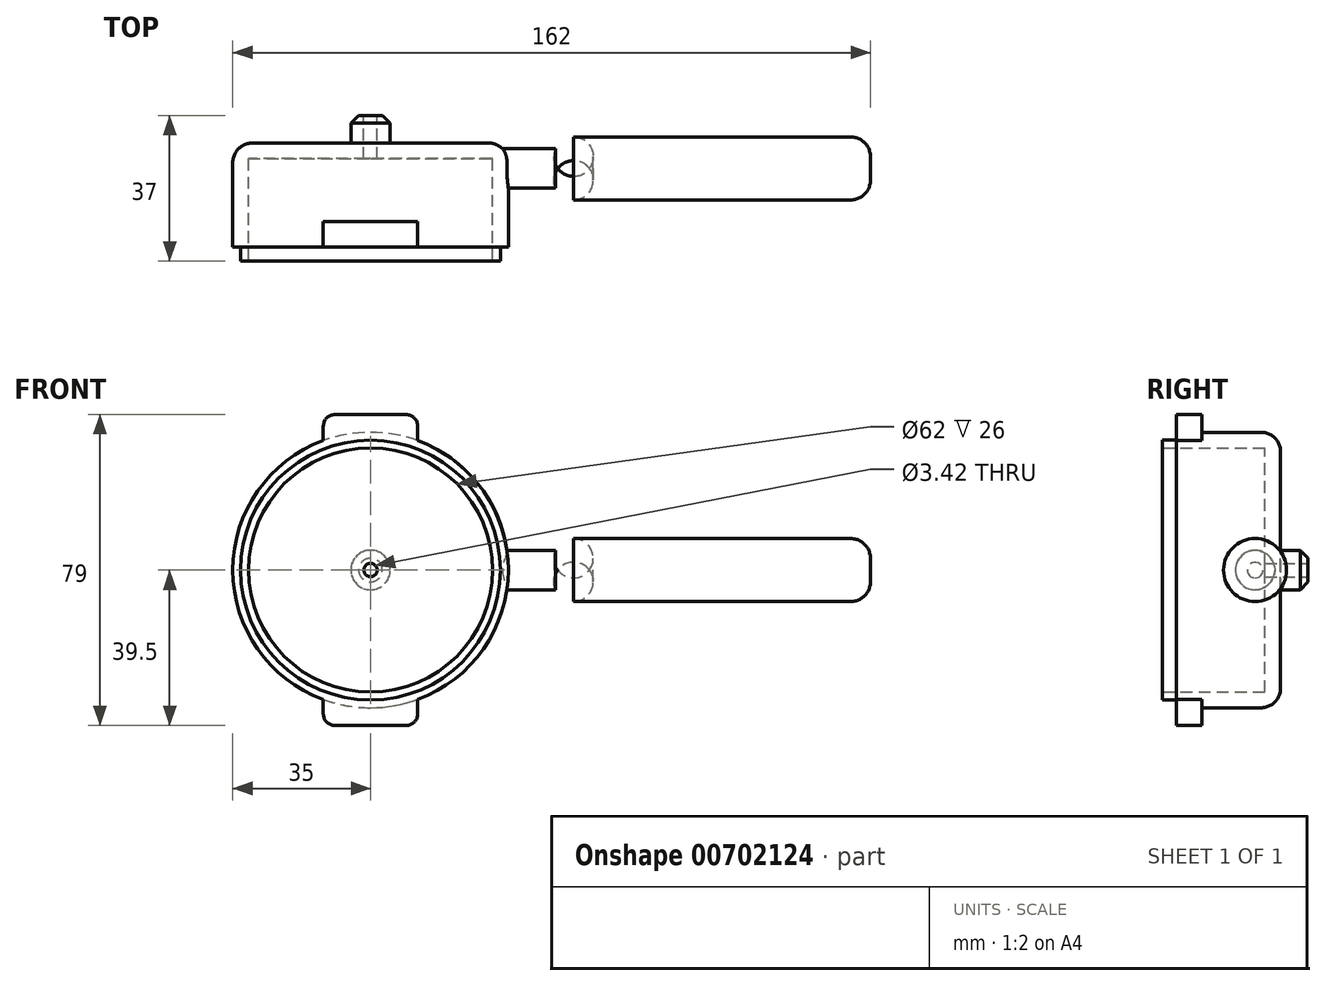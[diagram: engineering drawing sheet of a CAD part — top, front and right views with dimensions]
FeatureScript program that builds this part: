
annotation { "Feature Type Name" : "Feature", "Feature Type Description" : "" }
export const myFeature = defineFeature(function(context is Context, id is Id, definition is map)
    precondition{}
    {
        {
            var Q0;
            Q0=qCreatedBy(makeId("Front.planeOp"),FACE);
            var sketch = newSketch(context, id + "F0", { "sketchPlane" : qUnion([Q0])});
            skCircle(sketch, "E0", {"center": v(0, 0) * mm, "radius": 35 * mm});
            skSolve(sketch);
        }
        {
            var Q0;
            Q0=makeQuery(id+"F0.imprint","IMPRINT",FACE,{"disambiguationData":[TD([[makeQuery(id+"F0.imprint","IMPRINT",EDGE,{"derivedFrom":sQuery(id+"F0.wireOp",EDGE,"E0")}),1.0]])]});
            extrude(context, id + "F1", {"entities" : qUnion([Q0]), "depth" : 30 * mm, "offsetDistance" : 25 * mm});
        }
        {
            var Q0;
            Q0=makeQuery(id+"F1.opExtrude","CAP_FACE",FACE,{"disambiguationData":[OSD([sQuery(id+"F0.wireOp",EDGE,"E0")])],"isStart":false});
            shell(context, id + "F2", {"entities" : qUnion([Q0]), "thickness" : 4 * mm});
        }
        {
            var Q0;
            Q0=makeQuery(id+"F1.opExtrude","CAP_EDGE",EDGE,{"disambiguationData":[OSD([sQuery(id+"F0.wireOp",EDGE,"E0")])],"isStart":true});
            fillet(context, id + "F3", {"entities" : qUnion([Q0]), "radius" : 5 * mm, "tangentPropagation" : true, "allowEdgeOverflow" : false});
        }
        {
            var Q0;
            Q0=qCreatedBy(makeId("Right.planeOp"),FACE);
            cPlane(context, id + "F4", {"entities" : qUnion([Q0]), "cplaneType" : CPlaneType.OFFSET, "offset" : 47 * mm, "width" : 150 * mm, "height" : 150 * mm});
        }
        {
            var Q0;
            Q0=qCreatedBy(id+"F4.planeOp",FACE);
            var sketch = newSketch(context, id + "F5", { "sketchPlane" : qUnion([Q0])});
            skCircle(sketch, "E1", {"center": v(-6.47, 0) * mm, "radius": 5 * mm});
            skSolve(sketch);
        }
        {
            var Q0;
            Q0=makeQuery(id+"F5.imprint","IMPRINT",FACE,{"disambiguationData":[TD([[makeQuery(id+"F5.imprint","IMPRINT",EDGE,{"derivedFrom":sQuery(id+"F5.wireOp",EDGE,"E1")}),1.0]])]});
            extrude(context, id + "F6", {"entities" : qUnion([Q0]), "operationType" : NewBodyOperationType.ADD, "endBound" : BoundingType.UP_TO_NEXT, "oppositeDirection" : true, "depth" : 25 * mm, "offsetDistance" : 25 * mm});
        }
        {
            var Q0;
            Q0=makeQuery(id+"F6.opExtrude","CAP_FACE",FACE,{"disambiguationData":[OSD([sQuery(id+"F5.wireOp",EDGE,"E1")])],"isStart":true});
            var sketch = newSketch(context, id + "F7", { "sketchPlane" : qUnion([Q0])});
            skCircle(sketch, "E2", {"center": v(-6.47, 0) * mm, "radius": 8 * mm});
            skSolve(sketch);
        }
        {
            var Q0;
            Q0=makeQuery(id+"F7.imprint","IMPRINT",FACE,{"disambiguationData":[TD([[makeQuery(id+"F7.imprint","IMPRINT",EDGE,{"derivedFrom":makeQuery(id+"F6.opExtrude","CAP_EDGE",EDGE,{"disambiguationData":[OSD([sQuery(id+"F5.wireOp",EDGE,"E1")])],"isStart":true})}),1.0]])]});
            var Q1;
            Q1=makeQuery(id+"F7.imprint","IMPRINT",FACE,{"disambiguationData":[TD([[makeQuery(id+"F7.imprint","IMPRINT",EDGE,{"derivedFrom":sQuery(id+"F7.wireOp",EDGE,"E2")}),1.0]])]});
            extrude(context, id + "F8", {"entities" : qUnion([Q0, Q1]), "operationType" : NewBodyOperationType.ADD, "depth" : 80 * mm, "offsetDistance" : 25 * mm});
        }
        {
            var Q0;
            Q0=makeQuery(id+"F1.opExtrude","CAP_FACE",FACE,{"disambiguationData":[OSD([sQuery(id+"F0.wireOp",EDGE,"E0")])],"isStart":true});
            var sketch = newSketch(context, id + "F9", { "sketchPlane" : qUnion([Q0])});
            skCircle(sketch, "E3", {"center": v(0, 0) * mm, "radius": 5 * mm});
            skSolve(sketch);
        }
        {
            var Q0;
            Q0=makeQuery(id+"F9.imprint","IMPRINT",FACE,{"disambiguationData":[TD([[makeQuery(id+"F9.imprint","IMPRINT",EDGE,{"derivedFrom":sQuery(id+"F9.wireOp",EDGE,"E3")}),1.0]])]});
            extrude(context, id + "F10", {"entities" : qUnion([Q0]), "operationType" : NewBodyOperationType.ADD, "depth" : 7 * mm, "offsetDistance" : 25 * mm});
        }
        {
            var Q0;
            Q0=makeQuery(id+"F10.opExtrude","CAP_EDGE",EDGE,{"disambiguationData":[OSD([sQuery(id+"F9.wireOp",EDGE,"E3")])],"isStart":false});
            chamfer(context, id + "F11", {"entities" : qUnion([Q0]), "width" : 2 * mm, "tangentPropagation" : true});
        }
        {
            var Q0;
            Q0=makeQuery(id+"F1.opExtrude","CAP_FACE",FACE,{"disambiguationData":[OSD([sQuery(id+"F0.wireOp",EDGE,"E0")])],"isStart":false});
            cPlane(context, id + "F12", {"entities" : qUnion([Q0]), "cplaneType" : CPlaneType.OFFSET, "offset" : 3.5 * mm, "oppositeDirection" : true, "width" : 150 * mm, "height" : 150 * mm});
        }
        {
            var Q0;
            Q0=qCreatedBy(id+"F12.planeOp",FACE);
            var sketch = newSketch(context, id + "F13", { "sketchPlane" : qUnion([Q0])});
            skArc(sketch, "E4.0", {"start": v(12, 32.88) * mm, "mid": v(0, 35) * mm, "end": v(-12, 32.88) * mm});
            skLineSegment(sketch, "E5", {"start": v(0, 0) * mm, "end": v(-35, 0) * mm});
            skLineSegment(sketch, "E6", {"start": v(12, 39.5) * mm, "end": v(-12, 39.5) * mm});
            skLineSegment(sketch, "E7", {"start": v(12, 39.5) * mm, "end": v(12, 32.88) * mm});
            skLineSegment(sketch, "E8", {"start": v(-12, 39.5) * mm, "end": v(-12, 32.88) * mm});
            skPoint(sketch, "E9.orphan", {"position": v(3.01, 0) * mm});
            skLineSegment(sketch, "E10.MirrorCS", {"start": v(12, -39.5) * mm, "end": v(12, -32.88) * mm});
            skLineSegment(sketch, "E11.MirrorCS", {"start": v(12, -39.5) * mm, "end": v(-12, -39.5) * mm});
            skLineSegment(sketch, "E12.MirrorCS", {"start": v(-12, -39.5) * mm, "end": v(-12, -32.88) * mm});
            skArc(sketch, "E13.MirrorCS", {"start": v(12, -32.88) * mm, "mid": v(0, -35) * mm, "end": v(-12, -32.88) * mm});
            skSolve(sketch);
        }
        {
            var Q0;
            Q0=makeQuery(id+"F13.imprint","IMPRINT",FACE,{"disambiguationData":[TD([[makeQuery(id+"F13.imprint","IMPRINT",EDGE,{"derivedFrom":sQuery(id+"F13.wireOp",EDGE,"E10.MirrorCS")}),1.0]])]});
            var Q1;
            Q1=makeQuery(id+"F13.imprint","IMPRINT",FACE,{"disambiguationData":[TD([[makeQuery(id+"F13.imprint","IMPRINT",EDGE,{"derivedFrom":sQuery(id+"F13.wireOp",EDGE,"E4.0")}),-1.0]])]});
            extrude(context, id + "F14", {"entities" : qUnion([Q0, Q1]), "operationType" : NewBodyOperationType.ADD, "oppositeDirection" : true, "depth" : 6.5 * mm, "offsetDistance" : 25 * mm});
        }
        {
            var Q0;
            Q0=makeQuery(id+"F8.opExtrude","CAP_EDGE",EDGE,{"disambiguationData":[OSD([sQuery(id+"F7.wireOp",EDGE,"E2")])],"isStart":false});
            fillet(context, id + "F15", {"entities" : qUnion([Q0]), "radius" : 5 * mm, "tangentPropagation" : true, "allowEdgeOverflow" : false});
        }
        {
            var Q0;
            Q0=makeQuery(id+"F8.opExtrude","CAP_EDGE",EDGE,{"disambiguationData":[OSD([sQuery(id+"F7.wireOp",EDGE,"E2")])],"isStart":true});
            fillet(context, id + "F16", {"entities" : qUnion([Q0]), "radius" : 5 * mm, "tangentPropagation" : true, "allowEdgeOverflow" : false});
        }
        {
            var Q0;
            Q0=makeQuery(id+"F1.opExtrude","CAP_FACE",FACE,{"disambiguationData":[OSD([sQuery(id+"F0.wireOp",EDGE,"E0")])],"isStart":false});
            var sketch = newSketch(context, id + "F17", { "sketchPlane" : qUnion([Q0])});
            skCircle(sketch, "E14", {"center": v(0, 0) * mm, "radius": 33 * mm});
            skCircle(sketch, "E15.0", {"center": v(0, 0) * mm, "radius": 35 * mm});
            skSolve(sketch);
        }
        {
            var Q0;
            Q0=makeQuery(id+"F17.imprint","IMPRINT",FACE,{"disambiguationData":[TD([[makeQuery(id+"F17.imprint","IMPRINT",EDGE,{"derivedFrom":sQuery(id+"F17.wireOp",EDGE,"E14")}),-1.0]])]});
            var Q1;
            Q1=makeQuery(id+"F14.opExtrude","CAP_FACE",FACE,{"disambiguationData":[OSD([sQuery(id+"F13.wireOp",EDGE,"E4.0"),sQuery(id+"F13.wireOp",EDGE,"E6"),sQuery(id+"F13.wireOp",EDGE,"E7"),sQuery(id+"F13.wireOp",EDGE,"E8")])],"isStart":true});
            extrude(context, id + "F18", {"entities" : qUnion([Q0]), "operationType" : NewBodyOperationType.REMOVE, "endBound" : BoundingType.UP_TO_SURFACE, "oppositeDirection" : true, "depth" : 25 * mm, "endBoundEntityFace" : qUnion([Q1]), "offsetDistance" : 25 * mm});
        }
        {
            var Q0;
            Q0=makeQuery(id+"F14.opExtrude","SWEPT_EDGE",EDGE,{"disambiguationData":[OSD([sQuery(id+"F13.wireOp",EDGE,"E6"),sQuery(id+"F13.wireOp",EDGE,"E7")])]});
            var Q1;
            Q1=makeQuery(id+"F14.opExtrude","SWEPT_EDGE",EDGE,{"disambiguationData":[OSD([sQuery(id+"F13.wireOp",EDGE,"E6"),sQuery(id+"F13.wireOp",EDGE,"E8")])]});
            var Q2;
            Q2=makeQuery(id+"F14.opExtrude","SWEPT_EDGE",EDGE,{"disambiguationData":[OSD([sQuery(id+"F13.wireOp",EDGE,"E11.MirrorCS"),sQuery(id+"F13.wireOp",EDGE,"E12.MirrorCS")])]});
            var Q3;
            Q3=makeQuery(id+"F14.opExtrude","SWEPT_EDGE",EDGE,{"disambiguationData":[OSD([sQuery(id+"F13.wireOp",EDGE,"E10.MirrorCS"),sQuery(id+"F13.wireOp",EDGE,"E11.MirrorCS")])]});
            fillet(context, id + "F19", {"entities" : qUnion([Q0, Q1, Q2, Q3]), "radius" : 3 * mm, "tangentPropagation" : true, "allowEdgeOverflow" : false});
        }
        {
            var Q0;
            Q0=makeQuery(id+"F10.opExtrude","CAP_FACE",FACE,{"disambiguationData":[OSD([sQuery(id+"F9.wireOp",EDGE,"E3")])],"isStart":false});
            var sketch = newSketch(context, id + "F20", { "sketchPlane" : qUnion([Q0])});
            skCircle(sketch, "E16", {"center": v(0, 0) * mm, "radius": 1.7 * mm});
            skSolve(sketch);
        }
        {
            var Q0;
            Q0=makeQuery(id+"F20.imprint","IMPRINT",FACE,{"disambiguationData":[TD([[makeQuery(id+"F20.imprint","IMPRINT",EDGE,{"derivedFrom":sQuery(id+"F20.wireOp",EDGE,"E16")}),1.0]])]});
            extrude(context, id + "F21", {"entities" : qUnion([Q0]), "operationType" : NewBodyOperationType.REMOVE, "endBound" : BoundingType.THROUGH_ALL, "oppositeDirection" : true, "depth" : 25 * mm, "offsetDistance" : 25 * mm});
        }
    });
